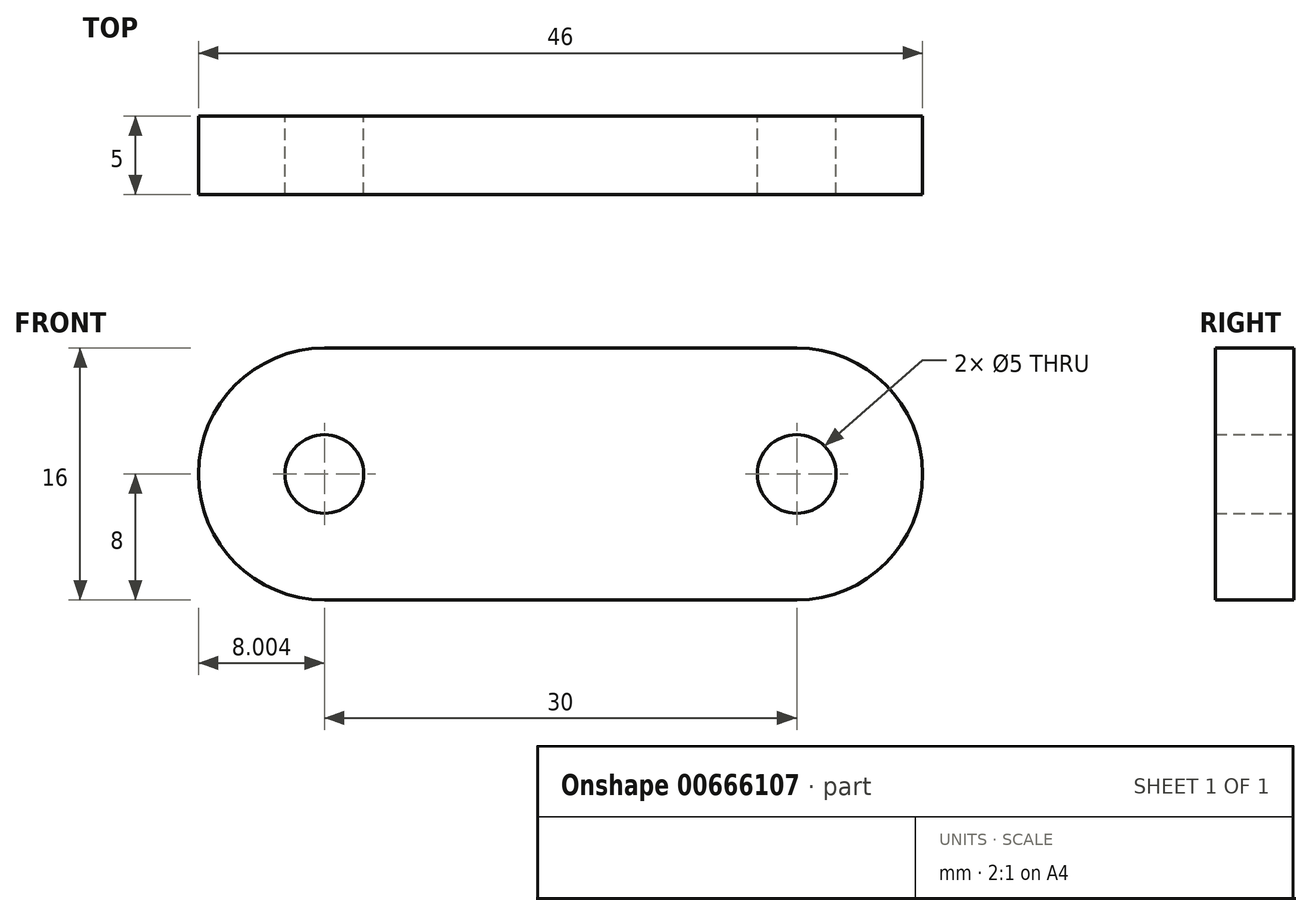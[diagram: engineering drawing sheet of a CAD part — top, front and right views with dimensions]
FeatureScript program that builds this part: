
annotation { "Feature Type Name" : "Feature", "Feature Type Description" : "" }
export const myFeature = defineFeature(function(context is Context, id is Id, definition is map)
    precondition{}
    {
        {
            var Q0;
            Q0=qCreatedBy(makeId("Front.planeOp"),FACE);
            var sketch = newSketch(context, id + "F0", { "sketchPlane" : qUnion([Q0])});
            skLineSegment(sketch, "E0.bottom", {"start": v(-11.23, 8) * mm, "end": v(18.77, 8) * mm});
            skLineSegment(sketch, "E0.top", {"start": v(-11.23, -8) * mm, "end": v(18.77, -8) * mm});
            skArc(sketch, "E1", {"start": v(-11.23, 8) * mm, "mid": v(-19.23, 0) * mm, "end": v(-11.23, -8) * mm});
            skArc(sketch, "E2", {"start": v(18.77, -8) * mm, "mid": v(26.77, 0) * mm, "end": v(18.77, 8) * mm});
            skCircle(sketch, "E3", {"center": v(-11.23, 0) * mm, "radius": 2.5 * mm});
            skCircle(sketch, "E4", {"center": v(18.77, 0) * mm, "radius": 2.5 * mm});
            skSolve(sketch);
        }
        {
            var Q0;
            Q0=makeQuery(id+"F0.imprint","IMPRINT",FACE,{"disambiguationData":[TD([[makeQuery(id+"F0.imprint","IMPRINT",EDGE,{"derivedFrom":sQuery(id+"F0.wireOp",EDGE,"E0.bottom")}),-1.0]])]});
            extrude(context, id + "F1", {"entities" : qUnion([Q0]), "depth" : 5 * mm, "offsetDistance" : 25 * mm});
        }
    });
